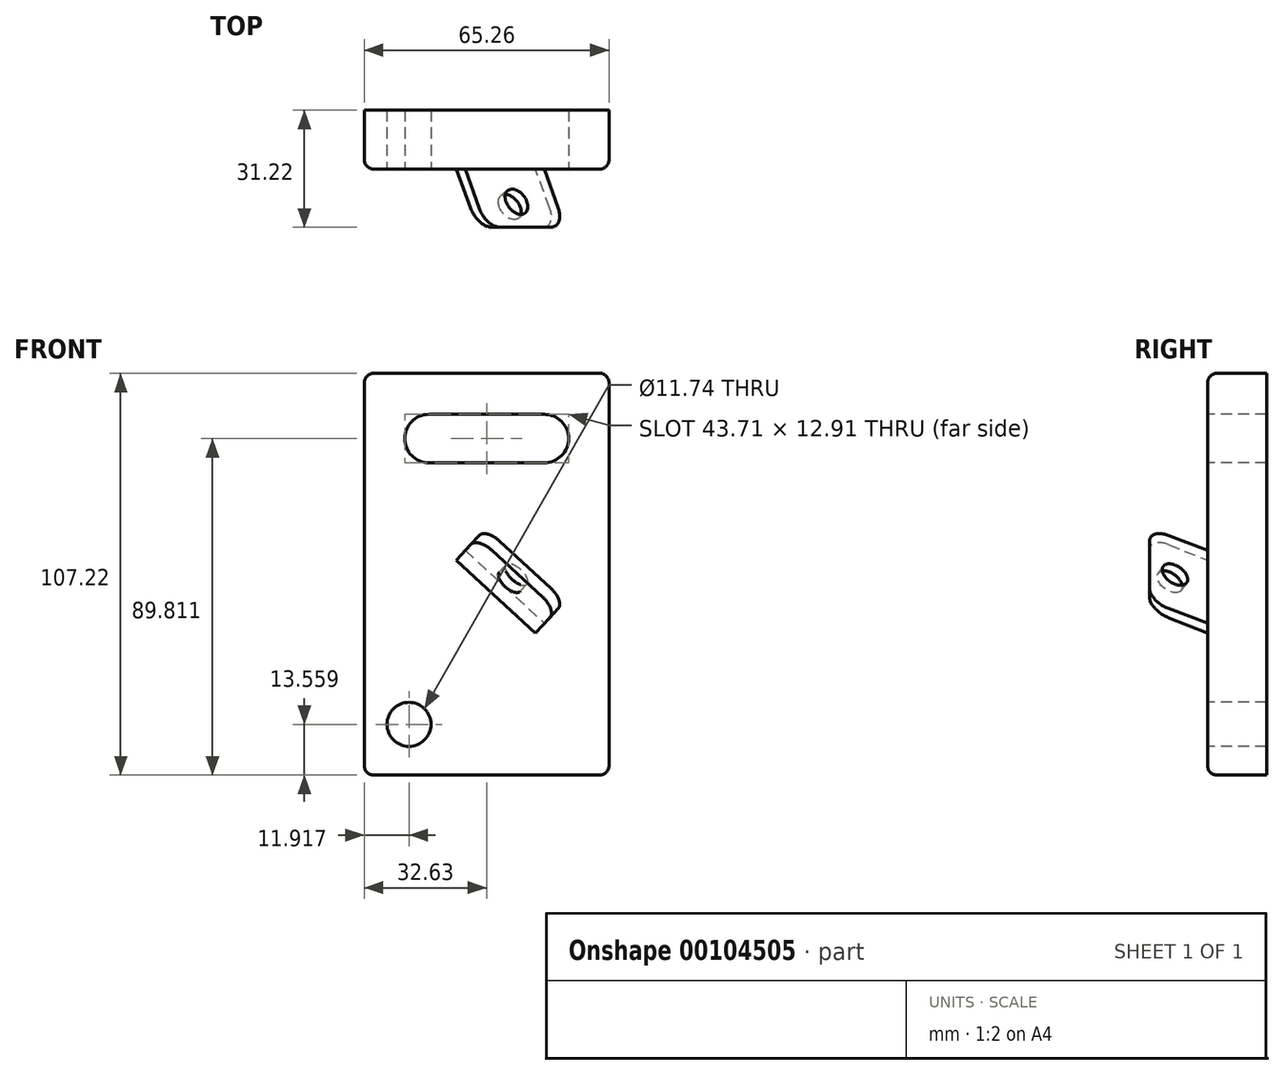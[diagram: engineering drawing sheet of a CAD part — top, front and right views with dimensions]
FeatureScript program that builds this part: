
annotation { "Feature Type Name" : "Feature", "Feature Type Description" : "" }
export const myFeature = defineFeature(function(context is Context, id is Id, definition is map)
    precondition{}
    {
        {
            var Q0;
            Q0=qCreatedBy(makeId("Front.planeOp"),FACE);
            var sketch = newSketch(context, id + "F0", { "sketchPlane" : qUnion([Q0])});
            skLineSegment(sketch, "E0.bottom", {"start": v(32.63, 53.61) * mm, "end": v(-32.63, 53.61) * mm});
            skLineSegment(sketch, "E0.top", {"start": v(32.63, -53.61) * mm, "end": v(-32.63, -53.61) * mm});
            skLineSegment(sketch, "E0.left", {"start": v(32.63, 53.61) * mm, "end": v(32.63, -53.61) * mm});
            skLineSegment(sketch, "E0.right", {"start": v(-32.63, 53.61) * mm, "end": v(-32.63, -53.61) * mm});
            skPoint(sketch, "E0.middle", {"position": v(0, 0) * mm});
            skSolve(sketch);
        }
        {
            var Q0;
            Q0 = qSketchRegion(id + "F0", true);
            extrude(context, id + "F1", {"entities" : qUnion([Q0]), "endBound" : BoundingType.SYMMETRIC, "depth" : 15.72 * mm});
        }
        {
            var Q0;
            Q0=makeQuery(id+"F1.opExtrude","CAP_FACE",FACE,{"disambiguationData":[OSD([sQuery(id+"F0.wireOp",EDGE,"E0.bottom"),sQuery(id+"F0.wireOp",EDGE,"E0.top"),sQuery(id+"F0.wireOp",EDGE,"E0.left"),sQuery(id+"F0.wireOp",EDGE,"E0.right")])],"isStart":false});
            var sketch = newSketch(context, id + "F2", { "sketchPlane" : qUnion([Q0])});
            skArc(sketch, "E1", {"start": v(-15.4, 42.66) * mm, "mid": v(-21.85, 36.2) * mm, "end": v(-15.4, 29.74) * mm});
            skArc(sketch, "E2.MirrorC", {"start": v(15.4, 42.66) * mm, "mid": v(21.85, 36.2) * mm, "end": v(15.4, 29.74) * mm});
            skLineSegment(sketch, "E3", {"start": v(-15.4, 42.66) * mm, "end": v(15.4, 42.66) * mm});
            skLineSegment(sketch, "E4", {"start": v(-15.4, 29.74) * mm, "end": v(15.4, 29.74) * mm});
            skCircle(sketch, "E5", {"center": v(-20.71, -40.05) * mm, "radius": 5.87 * mm});
            skSolve(sketch);
        }
        {
            var Q0;
            Q0 = qSketchRegion(id + "F2", true);
            extrude(context, id + "F3", {"entities" : qUnion([Q0]), "operationType" : NewBodyOperationType.REMOVE, "oppositeDirection" : true, "depth" : 60.3 * mm});
        }
        {
            var Q0;
            Q0 = qSketchRegion(id + "F2", true);
            extrude(context, id + "F4", {"entities" : qUnion([Q0]), "operationType" : NewBodyOperationType.REMOVE, "oppositeDirection" : true, "depth" : 65.8 * mm});
        }
        {
            var Q0;
            Q0=makeQuery(id+"F1.opExtrude","SWEPT_EDGE",EDGE,{"disambiguationData":[OSD([sQuery(id+"F0.wireOp",EDGE,"E0.bottom"),sQuery(id+"F0.wireOp",EDGE,"E0.right")])]});
            var Q1;
            Q1=makeQuery(id+"F1.opExtrude","SWEPT_EDGE",EDGE,{"disambiguationData":[OSD([sQuery(id+"F0.wireOp",EDGE,"E0.bottom"),sQuery(id+"F0.wireOp",EDGE,"E0.left")])]});
            var Q2;
            Q2=makeQuery(id+"F1.opExtrude","SWEPT_EDGE",EDGE,{"disambiguationData":[OSD([sQuery(id+"F0.wireOp",EDGE,"E0.top"),sQuery(id+"F0.wireOp",EDGE,"E0.left")])]});
            var Q3;
            Q3=makeQuery(id+"F1.opExtrude","SWEPT_EDGE",EDGE,{"disambiguationData":[OSD([sQuery(id+"F0.wireOp",EDGE,"E0.top"),sQuery(id+"F0.wireOp",EDGE,"E0.right")])]});
            var Q4;
            Q4=makeQuery(id+"F1.opExtrude","CAP_EDGE",EDGE,{"disambiguationData":[OSD([sQuery(id+"F0.wireOp",EDGE,"E0.right")])],"isStart":false});
            var Q5;
            Q5=makeQuery(id+"F1.opExtrude","CAP_EDGE",EDGE,{"disambiguationData":[OSD([sQuery(id+"F0.wireOp",EDGE,"E0.bottom")])],"isStart":false});
            var Q6;
            Q6=makeQuery(id+"F1.opExtrude","CAP_EDGE",EDGE,{"disambiguationData":[OSD([sQuery(id+"F0.wireOp",EDGE,"E0.left")])],"isStart":false});
            var Q7;
            Q7=makeQuery(id+"F1.opExtrude","CAP_EDGE",EDGE,{"disambiguationData":[OSD([sQuery(id+"F0.wireOp",EDGE,"E0.top")])],"isStart":false});
            fillet(context, id + "F5", {"entities" : qUnion([Q0, Q1, Q2, Q3, Q4, Q5, Q6, Q7]), "radius" : 2.54 * mm, "tangentPropagation" : true, "allowEdgeOverflow" : false});
        }
        {
            var Q0;
            Q0=makeQuery(id+"F1.opExtrude","CAP_FACE",FACE,{"disambiguationData":[OSD([sQuery(id+"F0.wireOp",EDGE,"E0.bottom"),sQuery(id+"F0.wireOp",EDGE,"E0.top"),sQuery(id+"F0.wireOp",EDGE,"E0.left"),sQuery(id+"F0.wireOp",EDGE,"E0.right")])],"isStart":false});
            var sketch = newSketch(context, id + "F6", { "sketchPlane" : qUnion([Q0])});
            skLineSegment(sketch, "E6", {"start": v(-9.57, -19.03) * mm, "end": v(12.53, 4.93) * mm});
            skSolve(sketch);
        }
        {
            var Q0;
            Q0=sQuery(id+"F6.wireOp",EDGE,"E6");
            cPlane(context, id + "F7", {"entities" : qUnion([Q0]), "cplaneType" : CPlaneType.LINE_ANGLE, "offset" : 25.4 * mm, "angle" : 0 * degree, "width" : 152.4 * mm, "height" : 152.4 * mm});
        }
        {
            var Q0;
            Q0=qCreatedBy(id+"F7.planeOp",FACE);
            var sketch = newSketch(context, id + "F8", { "sketchPlane" : qUnion([Q0])});
            skLineSegment(sketch, "E7", {"start": v(-6.26, 0) * mm, "end": v(-23.36, 8.85) * mm});
            skLineSegment(sketch, "E8", {"start": v(-23.36, 8.85) * mm, "end": v(-23.36, 5.64) * mm});
            skLineSegment(sketch, "E9", {"start": v(-23.36, 5.64) * mm, "end": v(-6.42, -3.54) * mm});
            skLineSegment(sketch, "E10", {"start": v(-6.42, -3.54) * mm, "end": v(-6.26, 0) * mm});
            skSolve(sketch);
        }
        {
            var Q0;
            Q0 = qSketchRegion(id + "F8", true);
            extrude(context, id + "F9", {"entities" : qUnion([Q0]), "operationType" : NewBodyOperationType.ADD, "endBound" : BoundingType.SYMMETRIC, "depth" : 28.74 * mm});
        }
        {
            var Q0;
            Q0=makeQuery(id+"F9.opExtrude","CAP_EDGE",EDGE,{"disambiguationData":[OSD([sQuery(id+"F8.wireOp",EDGE,"E8")])],"isStart":true});
            var Q1;
            Q1=makeQuery(id+"F9.opExtrude","CAP_EDGE",EDGE,{"disambiguationData":[OSD([sQuery(id+"F8.wireOp",EDGE,"E8")])],"isStart":false});
            fillet(context, id + "F10", {"entities" : qUnion([Q0, Q1]), "radius" : 5.08 * mm, "tangentPropagation" : true, "allowEdgeOverflow" : false});
        }
        {
            var Q0;
            Q0=makeQuery(id+"F9.opExtrude","SWEPT_FACE",FACE,{"disambiguationData":[OSD([sQuery(id+"F8.wireOp",EDGE,"E9")])]});
            var sketch = newSketch(context, id + "F11", { "sketchPlane" : qUnion([Q0])});
            skCircle(sketch, "E11", {"center": v(12.28, 13.28) * mm, "radius": 3.8 * mm});
            skSolve(sketch);
        }
        {
            var Q0;
            Q0 = qSketchRegion(id + "F11", true);
            extrude(context, id + "F12", {"entities" : qUnion([Q0]), "operationType" : NewBodyOperationType.REMOVE, "oppositeDirection" : true, "depth" : 5.85 * mm});
        }
    });
